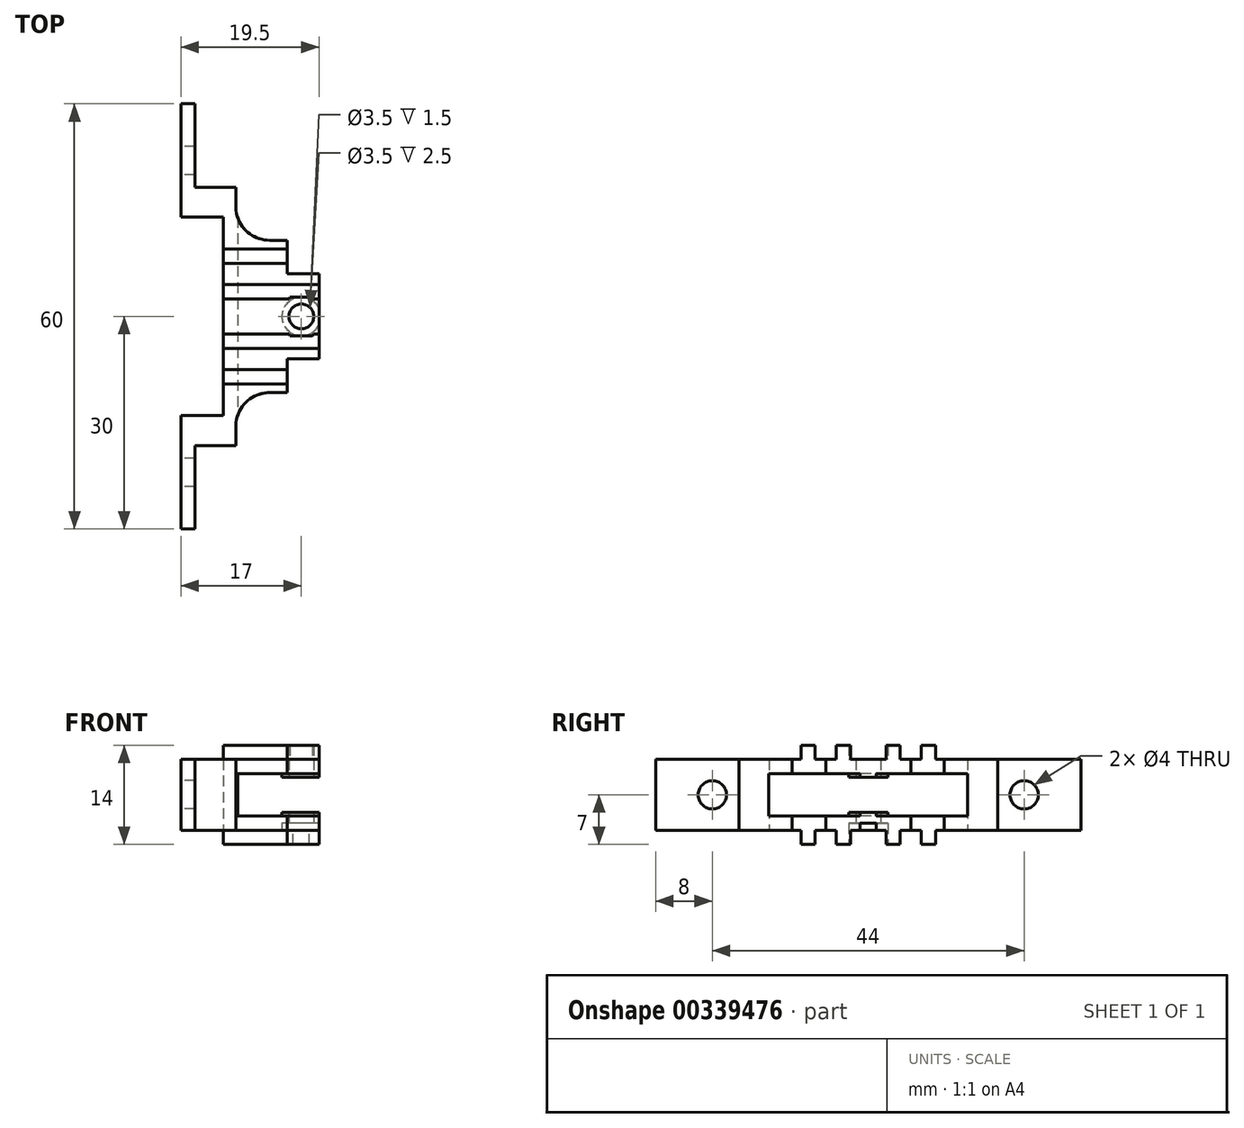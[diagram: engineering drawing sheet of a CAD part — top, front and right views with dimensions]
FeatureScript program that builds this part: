
annotation { "Feature Type Name" : "Feature", "Feature Type Description" : "" }
export const myFeature = defineFeature(function(context is Context, id is Id, definition is map)
    precondition{}
    {
        {
            var Q0;
            Q0=qCreatedBy(makeId("Top.planeOp"),FACE);
            var sketch = newSketch(context, id + "F0", { "sketchPlane" : qUnion([Q0])});
            skLineSegment(sketch, "E0.0", {"start": v(-988.73, -15.3) * mm, "end": v(-988.73, -19.06) * mm});
            skLineSegment(sketch, "E1.MirrorCS", {"start": v(19.5, -4.62) * mm, "end": v(19.5, -6) * mm});
            skLineSegment(sketch, "E2", {"start": v(19.5, -5.89) * mm, "end": v(19.5, 0.89) * mm});
            skLineSegment(sketch, "E3", {"start": v(15, -10.75) * mm, "end": v(15, -7) * mm});
            skLineSegment(sketch, "E4.MirrorCS", {"start": v(2, -30) * mm, "end": v(2, -18.25) * mm});
            skLineSegment(sketch, "E5.0", {"start": v(2, -18.25) * mm, "end": v(7.77, -18.25) * mm});
            skLineSegment(sketch, "E6.0", {"start": v(12.52, -10.75) * mm, "end": v(15, -10.75) * mm});
            skArc(sketch, "E7.0", {"start": v(12.52, -10.75) * mm, "mid": v(9.16, -12.14) * mm, "end": v(7.77, -15.5) * mm});
            skLineSegment(sketch, "E8.0", {"start": v(7.77, -15.5) * mm, "end": v(7.77, -18.25) * mm});
            skLineSegment(sketch, "E9", {"start": v(0, -30) * mm, "end": v(0, 0) * mm});
            skLineSegment(sketch, "E10", {"start": v(2, -30) * mm, "end": v(0, -30) * mm});
            skLineSegment(sketch, "E11.MirrorCS", {"start": v(2, 30) * mm, "end": v(2, 18.25) * mm});
            skLineSegment(sketch, "E12.MirrorCS", {"start": v(0, 30) * mm, "end": v(0, 0) * mm});
            skLineSegment(sketch, "E13.MirrorCS", {"start": v(2, 30) * mm, "end": v(0, 30) * mm});
            skLineSegment(sketch, "E14.MirrorCS", {"start": v(2, 18.25) * mm, "end": v(7.77, 18.25) * mm});
            skLineSegment(sketch, "E15.MirrorCS", {"start": v(7.77, 15.5) * mm, "end": v(7.77, 18.25) * mm});
            skArc(sketch, "E16.MirrorCS", {"start": v(12.52, 10.75) * mm, "mid": v(9.16, 12.14) * mm, "end": v(7.77, 15.5) * mm});
            skLineSegment(sketch, "E17.MirrorCS", {"start": v(12.52, 10.75) * mm, "end": v(15, 10.75) * mm});
            skLineSegment(sketch, "E18.MirrorCS", {"start": v(15, 10.75) * mm, "end": v(15, 7) * mm});
            skLineSegment(sketch, "E19.MirrorCS", {"start": v(19.5, 4.62) * mm, "end": v(19.5, 6) * mm});
            skLineSegment(sketch, "E20.MirrorCS", {"start": v(19.5, 5.89) * mm, "end": v(19.5, 0.89) * mm});
            skLineSegment(sketch, "E21", {"start": v(0, 7.5) * mm, "end": v(15, 7.5) * mm});
            skLineSegment(sketch, "E22", {"start": v(0, 4.5) * mm, "end": v(19.5, 4.5) * mm});
            skLineSegment(sketch, "E23", {"start": v(0, 9.5) * mm, "end": v(15, 9.5) * mm});
            skLineSegment(sketch, "E24", {"start": v(0, 2.5) * mm, "end": v(19.5, 2.5) * mm});
            skLineSegment(sketch, "E25", {"start": v(19.5, 6) * mm, "end": v(15, 6) * mm});
            skLineSegment(sketch, "E26", {"start": v(15, 6) * mm, "end": v(15, 10.75) * mm});
            skLineSegment(sketch, "E27.MirrorCS", {"start": v(0, -2.5) * mm, "end": v(19.5, -2.5) * mm});
            skLineSegment(sketch, "E28.MirrorCS", {"start": v(0, -4.5) * mm, "end": v(19.5, -4.5) * mm});
            skLineSegment(sketch, "E29.MirrorCS", {"start": v(0, -7.5) * mm, "end": v(15, -7.5) * mm});
            skLineSegment(sketch, "E30.MirrorCS", {"start": v(0, -9.5) * mm, "end": v(15, -9.5) * mm});
            skLineSegment(sketch, "E31.MirrorCS", {"start": v(19.5, -6) * mm, "end": v(15, -6) * mm});
            skLineSegment(sketch, "E32.MirrorCS", {"start": v(15, -6) * mm, "end": v(15, -10.75) * mm});
            skPoint(sketch, "E33.orphan", {"position": v(19.5, -0.89) * mm});
            skCircle(sketch, "E34", {"center": v(17, 0) * mm, "radius": 1.75 * mm});
            skCircle(sketch, "E35", {"center": v(17, 0) * mm, "radius": 2.75 * mm});
            skSolve(sketch);
        }
        {
            var Q0;
            Q0=makeQuery(id+"F0.imprint","IMPRINT",FACE,{"disambiguationData":[TD([[makeQuery(id+"F0.imprint","IMPRINT",EDGE,{"derivedFrom":sQuery(id+"F0.wireOp",EDGE,"E4.MirrorCS")}),1.0]])]});
            var Q1;
            Q1=makeQuery(id+"F0.imprint","IMPRINT",FACE,{"disambiguationData":[TD([[makeQuery(id+"F0.imprint","IMPRINT",EDGE,{"derivedFrom":sQuery(id+"F0.wireOp",EDGE,"E11.MirrorCS")}),-1.0]])]});
            var Q2;
            {var subQ4=sQuery(id+"F0.wireOp",EDGE,"E1.MirrorCS");Q2=makeQuery(id+"F0.imprint","IMPRINT",FACE,{"disambiguationData":[TD([[makeQuery(id+"F0.imprint","IMPRINT",EDGE,{"derivedFrom":subQ4}),-1.0]])]});}
            var Q3;
            {var subQ0=sQuery(id+"F0.wireOp",EDGE,"E27.MirrorCS");var subQ1=sQuery(id+"F0.wireOp",EDGE,"E2");var subQ2=makeQuery(id+"F0.imprint","INTERSECT",VERTEX,{"derivedFrom":[subQ1,subQ0]});Q3=makeQuery(id+"F0.imprint","IMPRINT",FACE,{"disambiguationData":[TD([[makeQuery(id+"F0.imprint","IMPRINT",EDGE,{"disambiguationData":[TD([[subQ2,-1.0]])],"derivedFrom":subQ1}),1.0]])]});}
            var Q4;
            {var subQ0=sQuery(id+"F0.wireOp",EDGE,"E29.MirrorCS");Q4=makeQuery(id+"F0.imprint","IMPRINT",FACE,{"disambiguationData":[TD([[makeQuery(id+"F0.imprint","IMPRINT",EDGE,{"derivedFrom":subQ0}),-1.0]])]});}
            var Q5;
            {var subQ0=sQuery(id+"F0.wireOp",EDGE,"E21");Q5=makeQuery(id+"F0.imprint","IMPRINT",FACE,{"disambiguationData":[TD([[makeQuery(id+"F0.imprint","IMPRINT",EDGE,{"derivedFrom":subQ0}),1.0]])]});}
            var Q6;
            {var subQ1=sQuery(id+"F0.wireOp",EDGE,"E19.MirrorCS");Q6=makeQuery(id+"F0.imprint","IMPRINT",FACE,{"disambiguationData":[TD([[makeQuery(id+"F0.imprint","IMPRINT",EDGE,{"derivedFrom":subQ1}),1.0]])]});}
            var Q7;
            {var subQ0=sQuery(id+"F0.wireOp",EDGE,"E24");var subQ1=sQuery(id+"F0.wireOp",EDGE,"E20.MirrorCS");var subQ2=makeQuery(id+"F0.imprint","INTERSECT",VERTEX,{"derivedFrom":[subQ1,subQ0]});Q7=makeQuery(id+"F0.imprint","IMPRINT",FACE,{"disambiguationData":[TD([[makeQuery(id+"F0.imprint","IMPRINT",EDGE,{"disambiguationData":[TD([[subQ2,-1.0]])],"derivedFrom":subQ1}),-1.0]])]});}
            var Q8;
            {var subQ1=sQuery(id+"F0.wireOp",EDGE,"E9");var subQ5=sQuery(id+"F0.wireOp",EDGE,"E12.MirrorCS");var subQ6=makeQuery(id+"F0.imprint","INTERSECT",VERTEX,{"derivedFrom":[subQ1,subQ5]});Q8=makeQuery(id+"F0.imprint","IMPRINT",FACE,{"disambiguationData":[TD([[makeQuery(id+"F0.imprint","IMPRINT",EDGE,{"disambiguationData":[TD([[subQ6,1.0]])],"derivedFrom":subQ1}),-1.0]])]});}
            var Q9;
            {var subQ7=sQuery(id+"F0.wireOp",EDGE,"E28.MirrorCS");Q9=makeQuery(id+"F0.imprint","IMPRINT",FACE,{"disambiguationData":[TD([[makeQuery(id+"F0.imprint","IMPRINT",EDGE,{"derivedFrom":subQ7}),1.0]])]});}
            var Q10;
            {var subQ0=sQuery(id+"F0.wireOp",EDGE,"E22");Q10=makeQuery(id+"F0.imprint","IMPRINT",FACE,{"disambiguationData":[TD([[makeQuery(id+"F0.imprint","IMPRINT",EDGE,{"derivedFrom":subQ0}),-1.0]])]});}
            var Q11;
            Q11=makeQuery(id+"F0.imprint","IMPRINT",FACE,{"disambiguationData":[TD([[makeQuery(id+"F0.imprint","IMPRINT",EDGE,{"derivedFrom":sQuery(id+"F0.wireOp",EDGE,"E34")}),-1.0]])]});
            var Q12;
            Q12=makeQuery(id+"F0.imprint","IMPRINT",FACE,{"disambiguationData":[TD([[makeQuery(id+"F0.imprint","IMPRINT",EDGE,{"derivedFrom":sQuery(id+"F0.wireOp",EDGE,"E34")}),-1.0]])]});
            extrude(context, id + "F1", {"entities" : qUnion([Q0, Q1, Q2, Q3, Q4, Q5, Q6, Q7, Q8, Q9, Q10, Q11, Q12]), "depth" : 2 * mm});
        }
        {
            var Q0;
            {var subQ0=sQuery(id+"F0.wireOp",EDGE,"E29.MirrorCS");Q0=makeQuery(id+"F0.imprint","IMPRINT",FACE,{"disambiguationData":[TD([[makeQuery(id+"F0.imprint","IMPRINT",EDGE,{"derivedFrom":subQ0}),-1.0]])]});}
            var Q1;
            {var subQ5=sQuery(id+"F0.wireOp",EDGE,"E28.MirrorCS");Q1=makeQuery(id+"F0.imprint","IMPRINT",FACE,{"disambiguationData":[TD([[makeQuery(id+"F0.imprint","IMPRINT",EDGE,{"derivedFrom":subQ5}),1.0]])]});}
            var Q2;
            {var subQ0=sQuery(id+"F0.wireOp",EDGE,"E22");Q2=makeQuery(id+"F0.imprint","IMPRINT",FACE,{"disambiguationData":[TD([[makeQuery(id+"F0.imprint","IMPRINT",EDGE,{"derivedFrom":subQ0}),-1.0]])]});}
            var Q3;
            {var subQ0=sQuery(id+"F0.wireOp",EDGE,"E21");Q3=makeQuery(id+"F0.imprint","IMPRINT",FACE,{"disambiguationData":[TD([[makeQuery(id+"F0.imprint","IMPRINT",EDGE,{"derivedFrom":subQ0}),1.0]])]});}
            extrude(context, id + "F2", {"entities" : qUnion([Q0, Q1, Q2, Q3]), "operationType" : NewBodyOperationType.ADD, "oppositeDirection" : true, "depth" : 2 * mm});
        }
        {
            var Q0;
            Q0=makeQuery(id+"F0.imprint","IMPRINT",FACE,{"disambiguationData":[TD([[makeQuery(id+"F0.imprint","IMPRINT",EDGE,{"derivedFrom":sQuery(id+"F0.wireOp",EDGE,"E34")}),-1.0]])]});
            var Q1;
            {var subQ0=sQuery(id+"F0.wireOp",EDGE,"E35");var subQ1=sQuery(id+"F0.wireOp",EDGE,"E27.MirrorCS");var subQ2=makeQuery(id+"F0.imprint","INTERSECT",VERTEX,{"disambiguationData":[OD(0.0)],"derivedFrom":[subQ1,subQ0]});Q1=makeQuery(id+"F0.imprint","IMPRINT",FACE,{"disambiguationData":[TD([[makeQuery(id+"F0.imprint","IMPRINT",EDGE,{"disambiguationData":[TD([[subQ2,-1.0]])],"derivedFrom":subQ1}),-1.0]])]});}
            var Q2;
            {var subQ0=sQuery(id+"F0.wireOp",EDGE,"E35");var subQ1=sQuery(id+"F0.wireOp",EDGE,"E24");var subQ2=makeQuery(id+"F0.imprint","INTERSECT",VERTEX,{"disambiguationData":[OD(0.0)],"derivedFrom":[subQ1,subQ0]});Q2=makeQuery(id+"F0.imprint","IMPRINT",FACE,{"disambiguationData":[TD([[makeQuery(id+"F0.imprint","IMPRINT",EDGE,{"disambiguationData":[TD([[subQ2,-1.0]])],"derivedFrom":subQ1}),1.0]])]});}
            extrude(context, id + "F3", {"entities" : qUnion([Q0, Q1, Q2]), "operationType" : NewBodyOperationType.ADD, "depth" : 2.5 * mm});
        }
        {
            var Q0;
            Q0=makeQuery(id+"F1.opExtrude","CAP_FACE",FACE,{"disambiguationData":[OSD([sQuery(id+"F0.wireOp",EDGE,"E1.MirrorCS"),sQuery(id+"F0.wireOp",EDGE,"E2"),sQuery(id+"F0.wireOp",EDGE,"E4.MirrorCS"),sQuery(id+"F0.wireOp",EDGE,"E5.0"),sQuery(id+"F0.wireOp",EDGE,"E6.0"),sQuery(id+"F0.wireOp",EDGE,"E7.0"),sQuery(id+"F0.wireOp",EDGE,"E8.0"),sQuery(id+"F0.wireOp",EDGE,"E10"),sQuery(id+"F0.wireOp",EDGE,"E9"),sQuery(id+"F0.wireOp",EDGE,"E11.MirrorCS"),sQuery(id+"F0.wireOp",EDGE,"E12.MirrorCS"),sQuery(id+"F0.wireOp",EDGE,"E13.MirrorCS"),sQuery(id+"F0.wireOp",EDGE,"E14.MirrorCS"),sQuery(id+"F0.wireOp",EDGE,"E15.MirrorCS"),sQuery(id+"F0.wireOp",EDGE,"E16.MirrorCS"),sQuery(id+"F0.wireOp",EDGE,"E17.MirrorCS"),sQuery(id+"F0.wireOp",EDGE,"E19.MirrorCS"),sQuery(id+"F0.wireOp",EDGE,"E20.MirrorCS"),sQuery(id+"F0.wireOp",EDGE,"E24"),sQuery(id+"F0.wireOp",EDGE,"E25"),sQuery(id+"F0.wireOp",EDGE,"E26"),sQuery(id+"F0.wireOp",EDGE,"E27.MirrorCS"),sQuery(id+"F0.wireOp",EDGE,"E31.MirrorCS"),sQuery(id+"F0.wireOp",EDGE,"E32.MirrorCS"),sQuery(id+"F0.wireOp",EDGE,"E34"),sQuery(id+"F0.wireOp",EDGE,"E35")])],"isStart":false});
            var sketch = newSketch(context, id + "F4", { "sketchPlane" : qUnion([Q0])});
            skLineSegment(sketch, "E36.MirrorCS", {"start": v(19.5, -4.62) * mm, "end": v(19.5, -6) * mm});
            skLineSegment(sketch, "E37", {"start": v(19.5, -5.89) * mm, "end": v(19.5, 0.89) * mm});
            skLineSegment(sketch, "E38", {"start": v(15, -10.75) * mm, "end": v(15, -7) * mm});
            skLineSegment(sketch, "E39.MirrorCS", {"start": v(2, -30) * mm, "end": v(2, -18.25) * mm});
            skLineSegment(sketch, "E40.0", {"start": v(2, -18.25) * mm, "end": v(7.77, -18.25) * mm});
            skLineSegment(sketch, "E41.0", {"start": v(12.52, -10.75) * mm, "end": v(15, -10.75) * mm});
            skArc(sketch, "E42.0", {"start": v(12.52, -10.75) * mm, "mid": v(9.16, -12.14) * mm, "end": v(7.77, -15.5) * mm});
            skLineSegment(sketch, "E43.0", {"start": v(7.77, -15.5) * mm, "end": v(7.77, -18.25) * mm});
            skLineSegment(sketch, "E44", {"start": v(0, -30) * mm, "end": v(0, -13) * mm});
            skLineSegment(sketch, "E45", {"start": v(2, -30) * mm, "end": v(0, -30) * mm});
            skLineSegment(sketch, "E46.MirrorCS", {"start": v(2, 30) * mm, "end": v(2, 18.25) * mm});
            skLineSegment(sketch, "E47.MirrorCS", {"start": v(0, 30) * mm, "end": v(0, 13) * mm});
            skLineSegment(sketch, "E48.MirrorCS", {"start": v(2, 30) * mm, "end": v(0, 30) * mm});
            skLineSegment(sketch, "E49.MirrorCS", {"start": v(2, 18.25) * mm, "end": v(7.77, 18.25) * mm});
            skLineSegment(sketch, "E50.MirrorCS", {"start": v(7.77, 15.5) * mm, "end": v(7.77, 18.25) * mm});
            skArc(sketch, "E51.MirrorCS", {"start": v(12.52, 10.75) * mm, "mid": v(9.16, 12.14) * mm, "end": v(7.77, 15.5) * mm});
            skLineSegment(sketch, "E52.MirrorCS", {"start": v(12.52, 10.75) * mm, "end": v(15, 10.75) * mm});
            skLineSegment(sketch, "E53.MirrorCS", {"start": v(15, 10.75) * mm, "end": v(15, 7) * mm});
            skLineSegment(sketch, "E54.MirrorCS", {"start": v(19.5, 4.62) * mm, "end": v(19.5, 6) * mm});
            skLineSegment(sketch, "E55.MirrorCS", {"start": v(19.5, 5.89) * mm, "end": v(19.5, 0.89) * mm});
            skLineSegment(sketch, "E56", {"start": v(8, 7.5) * mm, "end": v(15, 7.5) * mm});
            skLineSegment(sketch, "E57", {"start": v(8, 4.5) * mm, "end": v(19.5, 4.5) * mm});
            skLineSegment(sketch, "E58", {"start": v(8, 9.5) * mm, "end": v(15, 9.5) * mm});
            skLineSegment(sketch, "E59", {"start": v(8, 2.5) * mm, "end": v(19.5, 2.5) * mm});
            skLineSegment(sketch, "E60", {"start": v(19.5, 6) * mm, "end": v(15, 6) * mm});
            skLineSegment(sketch, "E61", {"start": v(15, 6) * mm, "end": v(15, 10.75) * mm});
            skLineSegment(sketch, "E62.MirrorCS", {"start": v(8, -2.5) * mm, "end": v(19.5, -2.5) * mm});
            skLineSegment(sketch, "E63.MirrorCS", {"start": v(8, -4.5) * mm, "end": v(19.5, -4.5) * mm});
            skLineSegment(sketch, "E64.MirrorCS", {"start": v(8, -7.5) * mm, "end": v(15, -7.5) * mm});
            skLineSegment(sketch, "E65.MirrorCS", {"start": v(8, -9.5) * mm, "end": v(15, -9.5) * mm});
            skLineSegment(sketch, "E66.MirrorCS", {"start": v(19.5, -6) * mm, "end": v(15, -6) * mm});
            skLineSegment(sketch, "E67.MirrorCS", {"start": v(15, -6) * mm, "end": v(15, -10.75) * mm});
            skPoint(sketch, "E68.orphan", {"position": v(19.5, -0.89) * mm});
            skCircle(sketch, "E69", {"center": v(14.5, 0) * mm, "radius": 1.75 * mm});
            skCircle(sketch, "E70", {"center": v(14.5, 0) * mm, "radius": 2.75 * mm});
            skLineSegment(sketch, "E71", {"start": v(0, -13) * mm, "end": v(6, -13) * mm});
            skLineSegment(sketch, "E72.MirrorCS", {"start": v(0, 13) * mm, "end": v(6, 13) * mm});
            skLineSegment(sketch, "E73", {"start": v(6, 13) * mm, "end": v(6, -13) * mm});
            skLineSegment(sketch, "E74.0", {"start": v(8, 14.03) * mm, "end": v(8, -14.03) * mm});
            skSolve(sketch);
        }
        {
            var Q0;
            {var subQ0=sQuery(id+"F4.wireOp",EDGE,"E71");Q0=makeQuery(id+"F4.imprint","IMPRINT",FACE,{"disambiguationData":[TD([[makeQuery(id+"F4.imprint","IMPRINT",EDGE,{"derivedFrom":subQ0}),1.0]])]});}
            extrude(context, id + "F5", {"entities" : qUnion([Q0]), "operationType" : NewBodyOperationType.REMOVE, "oppositeDirection" : true, "depth" : 7 * mm});
        }
        {
            var Q0;
            Q0=makeQuery(id+"F4.imprint","IMPRINT",FACE,{"disambiguationData":[TD([[makeQuery(id+"F4.imprint","IMPRINT",EDGE,{"derivedFrom":sQuery(id+"F4.wireOp",EDGE,"E39.MirrorCS")}),1.0]])]});
            extrude(context, id + "F6", {"entities" : qUnion([Q0]), "operationType" : NewBodyOperationType.ADD, "depth" : 6 * mm});
        }
        {
            var Q0;
            Q0=makeQuery(id+"F6.opExtrude","CAP_FACE",FACE,{"disambiguationData":[OSD([sQuery(id+"F4.wireOp",EDGE,"E39.MirrorCS"),sQuery(id+"F4.wireOp",EDGE,"E40.0"),sQuery(id+"F4.wireOp",EDGE,"E42.0"),sQuery(id+"F4.wireOp",EDGE,"E43.0"),sQuery(id+"F4.wireOp",EDGE,"E45"),sQuery(id+"F4.wireOp",EDGE,"E44"),sQuery(id+"F4.wireOp",EDGE,"E46.MirrorCS"),sQuery(id+"F4.wireOp",EDGE,"E47.MirrorCS"),sQuery(id+"F4.wireOp",EDGE,"E48.MirrorCS"),sQuery(id+"F4.wireOp",EDGE,"E49.MirrorCS"),sQuery(id+"F4.wireOp",EDGE,"E50.MirrorCS"),sQuery(id+"F4.wireOp",EDGE,"E51.MirrorCS"),sQuery(id+"F4.wireOp",EDGE,"E71"),sQuery(id+"F4.wireOp",EDGE,"E72.MirrorCS"),sQuery(id+"F4.wireOp",EDGE,"E73"),sQuery(id+"F4.wireOp",EDGE,"E74.0")])],"isStart":false});
            var sketch = newSketch(context, id + "F7", { "sketchPlane" : qUnion([Q0])});
            skLineSegment(sketch, "E75.MirrorCS", {"start": v(19.5, -4.62) * mm, "end": v(19.5, -6) * mm});
            skLineSegment(sketch, "E76", {"start": v(19.5, -5.89) * mm, "end": v(19.5, 0.89) * mm});
            skLineSegment(sketch, "E77", {"start": v(15, -10.75) * mm, "end": v(15, -7) * mm});
            skLineSegment(sketch, "E78.MirrorCS", {"start": v(2, -30) * mm, "end": v(2, -18.25) * mm});
            skLineSegment(sketch, "E79.0", {"start": v(2, -18.25) * mm, "end": v(7.77, -18.25) * mm});
            skLineSegment(sketch, "E80.0", {"start": v(12.52, -10.75) * mm, "end": v(15, -10.75) * mm});
            skArc(sketch, "E81.0", {"start": v(12.52, -10.75) * mm, "mid": v(9.16, -12.14) * mm, "end": v(7.77, -15.5) * mm});
            skLineSegment(sketch, "E82.0", {"start": v(7.77, -15.5) * mm, "end": v(7.77, -18.25) * mm});
            skLineSegment(sketch, "E83", {"start": v(0, -30) * mm, "end": v(0, -13) * mm});
            skLineSegment(sketch, "E84", {"start": v(2, -30) * mm, "end": v(0, -30) * mm});
            skLineSegment(sketch, "E85.MirrorCS", {"start": v(2, 30) * mm, "end": v(2, 18.25) * mm});
            skLineSegment(sketch, "E86.MirrorCS", {"start": v(0, 30) * mm, "end": v(0, 13) * mm});
            skLineSegment(sketch, "E87.MirrorCS", {"start": v(2, 30) * mm, "end": v(0, 30) * mm});
            skLineSegment(sketch, "E88.MirrorCS", {"start": v(2, 18.25) * mm, "end": v(7.77, 18.25) * mm});
            skLineSegment(sketch, "E89.MirrorCS", {"start": v(7.77, 15.5) * mm, "end": v(7.77, 18.25) * mm});
            skArc(sketch, "E90.MirrorCS", {"start": v(12.52, 10.75) * mm, "mid": v(9.16, 12.14) * mm, "end": v(7.77, 15.5) * mm});
            skLineSegment(sketch, "E91.MirrorCS", {"start": v(12.52, 10.75) * mm, "end": v(15, 10.75) * mm});
            skLineSegment(sketch, "E92.MirrorCS", {"start": v(15, 10.75) * mm, "end": v(15, 7) * mm});
            skLineSegment(sketch, "E93.MirrorCS", {"start": v(19.5, 4.62) * mm, "end": v(19.5, 6) * mm});
            skLineSegment(sketch, "E94.MirrorCS", {"start": v(19.5, 5.89) * mm, "end": v(19.5, 0.89) * mm});
            skLineSegment(sketch, "E95", {"start": v(19.5, 6) * mm, "end": v(15, 6) * mm});
            skLineSegment(sketch, "E96", {"start": v(15, 6) * mm, "end": v(15, 10.75) * mm});
            skLineSegment(sketch, "E97.MirrorCS", {"start": v(19.5, -6) * mm, "end": v(15, -6) * mm});
            skLineSegment(sketch, "E98.MirrorCS", {"start": v(15, -6) * mm, "end": v(15, -10.75) * mm});
            skPoint(sketch, "E99.orphan", {"position": v(19.5, -0.89) * mm});
            skCircle(sketch, "E100", {"center": v(17, 0) * mm, "radius": 1.75 * mm});
            skCircle(sketch, "E101", {"center": v(17, 0) * mm, "radius": 2.75 * mm});
            skLineSegment(sketch, "E102", {"start": v(0, -13) * mm, "end": v(6, -13) * mm});
            skLineSegment(sketch, "E103.MirrorCS", {"start": v(0, 13) * mm, "end": v(6, 13) * mm});
            skLineSegment(sketch, "E104", {"start": v(6, 13) * mm, "end": v(6, -13) * mm});
            skSolve(sketch);
        }
        {
            var Q0;
            Q0=makeQuery(id+"F7.imprint","IMPRINT",FACE,{"disambiguationData":[TD([[makeQuery(id+"F7.imprint","IMPRINT",EDGE,{"derivedFrom":sQuery(id+"F7.wireOp",EDGE,"E78.MirrorCS")}),1.0]])]});
            var Q1;
            {var subQ6=sQuery(id+"F7.wireOp",EDGE,"E75.MirrorCS");Q1=makeQuery(id+"F7.imprint","IMPRINT",FACE,{"disambiguationData":[TD([[makeQuery(id+"F7.imprint","IMPRINT",EDGE,{"derivedFrom":subQ6}),-1.0]])]});}
            var Q2;
            Q2=makeQuery(id+"F7.imprint","IMPRINT",FACE,{"disambiguationData":[TD([[makeQuery(id+"F7.imprint","IMPRINT",EDGE,{"derivedFrom":sQuery(id+"F7.wireOp",EDGE,"E100")}),-1.0]])]});
            var Q3;
            Q3=makeQuery(id+"F7.imprint","IMPRINT",FACE,{"disambiguationData":[TD([[makeQuery(id+"F7.imprint","IMPRINT",EDGE,{"derivedFrom":sQuery(id+"F7.wireOp",EDGE,"E100")}),-1.0]])]});
            extrude(context, id + "F8", {"entities" : qUnion([Q0, Q1, Q2, Q3]), "operationType" : NewBodyOperationType.ADD, "depth" : 2 * mm});
        }
        {
            var Q0;
            Q0=makeQuery(id+"F7.imprint","IMPRINT",FACE,{"disambiguationData":[TD([[makeQuery(id+"F7.imprint","IMPRINT",EDGE,{"derivedFrom":sQuery(id+"F7.wireOp",EDGE,"E100")}),-1.0]])]});
            extrude(context, id + "F9", {"entities" : qUnion([Q0]), "operationType" : NewBodyOperationType.ADD, "oppositeDirection" : true, "depth" : 0.5 * mm});
        }
        {
            var Q0;
            Q0=makeQuery(id+"F8.opExtrude","CAP_FACE",FACE,{"disambiguationData":[OSD([sQuery(id+"F7.wireOp",EDGE,"E75.MirrorCS"),sQuery(id+"F7.wireOp",EDGE,"E76"),sQuery(id+"F7.wireOp",EDGE,"E78.MirrorCS"),sQuery(id+"F7.wireOp",EDGE,"E79.0"),sQuery(id+"F7.wireOp",EDGE,"E80.0"),sQuery(id+"F7.wireOp",EDGE,"E81.0"),sQuery(id+"F7.wireOp",EDGE,"E82.0"),sQuery(id+"F7.wireOp",EDGE,"E84"),sQuery(id+"F7.wireOp",EDGE,"E83"),sQuery(id+"F7.wireOp",EDGE,"E85.MirrorCS"),sQuery(id+"F7.wireOp",EDGE,"E86.MirrorCS"),sQuery(id+"F7.wireOp",EDGE,"E87.MirrorCS"),sQuery(id+"F7.wireOp",EDGE,"E88.MirrorCS"),sQuery(id+"F7.wireOp",EDGE,"E89.MirrorCS"),sQuery(id+"F7.wireOp",EDGE,"E90.MirrorCS"),sQuery(id+"F7.wireOp",EDGE,"E91.MirrorCS"),sQuery(id+"F7.wireOp",EDGE,"E93.MirrorCS"),sQuery(id+"F7.wireOp",EDGE,"E94.MirrorCS"),sQuery(id+"F7.wireOp",EDGE,"E95"),sQuery(id+"F7.wireOp",EDGE,"E96"),sQuery(id+"F7.wireOp",EDGE,"E97.MirrorCS"),sQuery(id+"F7.wireOp",EDGE,"E98.MirrorCS"),sQuery(id+"F7.wireOp",EDGE,"E100"),sQuery(id+"F7.wireOp",EDGE,"E102"),sQuery(id+"F7.wireOp",EDGE,"E103.MirrorCS"),sQuery(id+"F7.wireOp",EDGE,"E104")])],"isStart":false});
            var sketch = newSketch(context, id + "F10", { "sketchPlane" : qUnion([Q0])});
            skLineSegment(sketch, "E105.MirrorCS", {"start": v(19.5, -4.62) * mm, "end": v(19.5, -6) * mm});
            skLineSegment(sketch, "E106", {"start": v(19.5, -5.89) * mm, "end": v(19.5, 0.89) * mm});
            skLineSegment(sketch, "E107", {"start": v(15, -10.75) * mm, "end": v(15, -7) * mm});
            skLineSegment(sketch, "E108.MirrorCS", {"start": v(2, -30) * mm, "end": v(2, -18.25) * mm});
            skLineSegment(sketch, "E109.0", {"start": v(2, -18.25) * mm, "end": v(7.77, -18.25) * mm});
            skLineSegment(sketch, "E110.0", {"start": v(12.52, -10.75) * mm, "end": v(15, -10.75) * mm});
            skArc(sketch, "E111.0", {"start": v(12.52, -10.75) * mm, "mid": v(9.16, -12.14) * mm, "end": v(7.77, -15.5) * mm});
            skLineSegment(sketch, "E112.0", {"start": v(7.77, -15.5) * mm, "end": v(7.77, -18.25) * mm});
            skLineSegment(sketch, "E113", {"start": v(0, -30) * mm, "end": v(0, -13) * mm});
            skLineSegment(sketch, "E114", {"start": v(2, -30) * mm, "end": v(0, -30) * mm});
            skLineSegment(sketch, "E115.MirrorCS", {"start": v(2, 30) * mm, "end": v(2, 18.25) * mm});
            skLineSegment(sketch, "E116.MirrorCS", {"start": v(0, 30) * mm, "end": v(0, 13) * mm});
            skLineSegment(sketch, "E117.MirrorCS", {"start": v(2, 30) * mm, "end": v(0, 30) * mm});
            skLineSegment(sketch, "E118.MirrorCS", {"start": v(2, 18.25) * mm, "end": v(7.77, 18.25) * mm});
            skLineSegment(sketch, "E119.MirrorCS", {"start": v(7.77, 15.5) * mm, "end": v(7.77, 18.25) * mm});
            skArc(sketch, "E120.MirrorCS", {"start": v(12.52, 10.75) * mm, "mid": v(9.16, 12.14) * mm, "end": v(7.77, 15.5) * mm});
            skLineSegment(sketch, "E121.MirrorCS", {"start": v(12.52, 10.75) * mm, "end": v(15, 10.75) * mm});
            skLineSegment(sketch, "E122.MirrorCS", {"start": v(15, 10.75) * mm, "end": v(15, 7) * mm});
            skLineSegment(sketch, "E123.MirrorCS", {"start": v(19.5, 4.62) * mm, "end": v(19.5, 6) * mm});
            skLineSegment(sketch, "E124.MirrorCS", {"start": v(19.5, 5.89) * mm, "end": v(19.5, 0.89) * mm});
            skLineSegment(sketch, "E125", {"start": v(6, 7.5) * mm, "end": v(15, 7.5) * mm});
            skLineSegment(sketch, "E126", {"start": v(6, 4.5) * mm, "end": v(19.5, 4.5) * mm});
            skLineSegment(sketch, "E127", {"start": v(6, 9.5) * mm, "end": v(15, 9.5) * mm});
            skLineSegment(sketch, "E128", {"start": v(6, 2.5) * mm, "end": v(19.5, 2.5) * mm});
            skLineSegment(sketch, "E129", {"start": v(19.5, 6) * mm, "end": v(15, 6) * mm});
            skLineSegment(sketch, "E130", {"start": v(15, 6) * mm, "end": v(15, 10.75) * mm});
            skLineSegment(sketch, "E131.MirrorCS", {"start": v(6, -2.5) * mm, "end": v(19.5, -2.5) * mm});
            skLineSegment(sketch, "E132.MirrorCS", {"start": v(6, -4.5) * mm, "end": v(19.5, -4.5) * mm});
            skLineSegment(sketch, "E133.MirrorCS", {"start": v(6, -7.5) * mm, "end": v(15, -7.5) * mm});
            skLineSegment(sketch, "E134.MirrorCS", {"start": v(6, -9.5) * mm, "end": v(15, -9.5) * mm});
            skLineSegment(sketch, "E135.MirrorCS", {"start": v(19.5, -6) * mm, "end": v(15, -6) * mm});
            skLineSegment(sketch, "E136.MirrorCS", {"start": v(15, -6) * mm, "end": v(15, -10.75) * mm});
            skPoint(sketch, "E137.orphan", {"position": v(19.5, -0.89) * mm});
            skCircle(sketch, "E138", {"center": v(17, 0) * mm, "radius": 1.75 * mm});
            skLineSegment(sketch, "E139", {"start": v(0, -13) * mm, "end": v(6, -13) * mm});
            skLineSegment(sketch, "E140.MirrorCS", {"start": v(0, 13) * mm, "end": v(6, 13) * mm});
            skLineSegment(sketch, "E141", {"start": v(6, 13) * mm, "end": v(6, -13) * mm});
            skCircle(sketch, "E142.cCircle", {"center": v(17, 0) * mm, "radius": 3.18 * mm, "construction": true});
            skLineSegment(sketch, "E142.0", {"start": v(18.59, -2.75) * mm, "end": v(15.41, -2.75) * mm});
            skLineSegment(sketch, "E142.1", {"start": v(15.41, -2.75) * mm, "end": v(13.82, 0) * mm});
            skLineSegment(sketch, "E142.2", {"start": v(13.82, 0) * mm, "end": v(15.41, 2.75) * mm});
            skLineSegment(sketch, "E142.3", {"start": v(15.41, 2.75) * mm, "end": v(18.59, 2.75) * mm});
            skLineSegment(sketch, "E142.4", {"start": v(18.59, 2.75) * mm, "end": v(20.18, 0) * mm});
            skLineSegment(sketch, "E142.5", {"start": v(20.18, 0) * mm, "end": v(18.59, -2.75) * mm});
            skSolve(sketch);
        }
        {
            var Q0;
            {var subQ0=sQuery(id+"F10.wireOp",EDGE,"E125");Q0=makeQuery(id+"F10.imprint","IMPRINT",FACE,{"disambiguationData":[TD([[makeQuery(id+"F10.imprint","IMPRINT",EDGE,{"derivedFrom":subQ0}),1.0]])]});}
            var Q1;
            {var subQ5=sQuery(id+"F10.wireOp",EDGE,"E126");Q1=makeQuery(id+"F10.imprint","IMPRINT",FACE,{"disambiguationData":[TD([[makeQuery(id+"F10.imprint","IMPRINT",EDGE,{"derivedFrom":subQ5}),-1.0]])]});}
            var Q2;
            {var subQ0=sQuery(id+"F10.wireOp",EDGE,"E132.MirrorCS");Q2=makeQuery(id+"F10.imprint","IMPRINT",FACE,{"disambiguationData":[TD([[makeQuery(id+"F10.imprint","IMPRINT",EDGE,{"derivedFrom":subQ0}),1.0]])]});}
            var Q3;
            {var subQ0=sQuery(id+"F10.wireOp",EDGE,"E133.MirrorCS");Q3=makeQuery(id+"F10.imprint","IMPRINT",FACE,{"disambiguationData":[TD([[makeQuery(id+"F10.imprint","IMPRINT",EDGE,{"derivedFrom":subQ0}),-1.0]])]});}
            extrude(context, id + "F11", {"entities" : qUnion([Q0, Q1, Q2, Q3]), "operationType" : NewBodyOperationType.ADD, "depth" : 2 * mm});
        }
        {
            var Q0;
            {var subQ4=sQuery(id+"F0.wireOp",EDGE,"E27.MirrorCS");var subQ14=sQuery(id+"F0.wireOp",EDGE,"E13.MirrorCS");var subQ15=sQuery(id+"F0.wireOp",EDGE,"E12.MirrorCS");var subQ17=sQuery(id+"F0.wireOp",EDGE,"E9");Q0=makeQuery(id+"F8.boolean.opBoolean","MERGE",FACE,{"derivedFrom":[makeQuery(id+"F6.boolean.opBoolean","MERGE",FACE,{"derivedFrom":[makeQuery(id+"F5.boolean.opBoolean","SPLIT",FACE,{"disambiguationData":[TD([makeQuery(id+"F1.opExtrude","SWEPT_FACE",FACE,{"disambiguationData":[OSD([subQ14])]})])],"derivedFrom":makeQuery(id+"F2.boolean.opBoolean","MERGE",FACE,{"derivedFrom":[makeQuery(id+"F1.opExtrude","SWEPT_FACE",FACE,{"disambiguationData":[OSD([subQ17,subQ15])]}),makeQuery(id+"F2.opExtrude","SWEPT_FACE",FACE,{"disambiguationData":[OSD([subQ17]),TDD([makeQuery(id+"F0.imprint","IMPRINT",EDGE,{"disambiguationData":[TD([[makeQuery(id+"F0.imprint","INTERSECT",VERTEX,{"derivedFrom":[subQ17,sQuery(id+"F0.wireOp",EDGE,"E29.MirrorCS")]}),1.0]])],"derivedFrom":subQ17})])]}),makeQuery(id+"F2.opExtrude","SWEPT_FACE",FACE,{"disambiguationData":[OSD([subQ17]),TDD([makeQuery(id+"F0.imprint","IMPRINT",EDGE,{"disambiguationData":[TD([[makeQuery(id+"F0.imprint","INTERSECT",VERTEX,{"derivedFrom":[subQ17,subQ4]}),1.0]])],"derivedFrom":subQ17})])]}),makeQuery(id+"F2.opExtrude","SWEPT_FACE",FACE,{"disambiguationData":[OSD([subQ15]),TDD([makeQuery(id+"F0.imprint","IMPRINT",EDGE,{"disambiguationData":[TD([[makeQuery(id+"F0.imprint","INTERSECT",VERTEX,{"derivedFrom":[subQ15,sQuery(id+"F0.wireOp",EDGE,"E21")]}),1.0]])],"derivedFrom":subQ15})])]}),makeQuery(id+"F2.opExtrude","SWEPT_FACE",FACE,{"disambiguationData":[OSD([subQ15]),TDD([makeQuery(id+"F0.imprint","IMPRINT",EDGE,{"disambiguationData":[TD([[makeQuery(id+"F0.imprint","INTERSECT",VERTEX,{"derivedFrom":[subQ15,sQuery(id+"F0.wireOp",EDGE,"E22")]}),-1.0]])],"derivedFrom":subQ15})])]})]})}),makeQuery(id+"F6.opExtrude","SWEPT_FACE",FACE,{"disambiguationData":[OSD([sQuery(id+"F4.wireOp",EDGE,"E47.MirrorCS")])]})]}),makeQuery(id+"F8.opExtrude","SWEPT_FACE",FACE,{"disambiguationData":[OSD([sQuery(id+"F7.wireOp",EDGE,"E86.MirrorCS")])]})]});}
            var sketch = newSketch(context, id + "F12", { "sketchPlane" : qUnion([Q0])});
            skCircle(sketch, "E143", {"center": v(-22, 5) * mm, "radius": 2 * mm});
            skCircle(sketch, "E144.MirrorC", {"center": v(22, 5) * mm, "radius": 2 * mm});
            skSolve(sketch);
        }
        {
            var Q0;
            Q0=qSketchRegion(id+"F12",true);
            extrude(context, id + "F13", {"entities" : qUnion([Q0]), "operationType" : NewBodyOperationType.REMOVE, "oppositeDirection" : true, "depth" : 25 * mm});
        }
        {
            var Q0;
            {var subQ0=sQuery(id+"F0.wireOp",EDGE,"E35");var subQ1=sQuery(id+"F0.wireOp",EDGE,"E34");var subQ2=sQuery(id+"F0.wireOp",EDGE,"E27.MirrorCS");var subQ3=sQuery(id+"F0.wireOp",EDGE,"E9");var subQ5=sQuery(id+"F0.wireOp",EDGE,"E24");var subQ9=sQuery(id+"F0.wireOp",EDGE,"E2");var subQ10=sQuery(id+"F0.wireOp",EDGE,"E12.MirrorCS");var subQ11=sQuery(id+"F0.wireOp",EDGE,"E20.MirrorCS");var subQ15=sQuery(id+"F0.wireOp",EDGE,"E19.MirrorCS");var subQ16=sQuery(id+"F0.wireOp",EDGE,"E1.MirrorCS");Q0=makeQuery(id+"F3.boolean.opBoolean","MERGE",FACE,{"derivedFrom":[makeQuery(id+"F2.boolean.opBoolean","SPLIT",FACE,{"disambiguationData":[TD([makeQuery(id+"F1.opExtrude","SWEPT_FACE",FACE,{"disambiguationData":[OSD([subQ5])]})])],"derivedFrom":makeQuery(id+"F1.opExtrude","CAP_FACE",FACE,{"disambiguationData":[OSD([subQ16,subQ9,sQuery(id+"F0.wireOp",EDGE,"E4.MirrorCS"),sQuery(id+"F0.wireOp",EDGE,"E5.0"),sQuery(id+"F0.wireOp",EDGE,"E6.0"),sQuery(id+"F0.wireOp",EDGE,"E7.0"),sQuery(id+"F0.wireOp",EDGE,"E8.0"),sQuery(id+"F0.wireOp",EDGE,"E10"),subQ3,sQuery(id+"F0.wireOp",EDGE,"E11.MirrorCS"),subQ10,sQuery(id+"F0.wireOp",EDGE,"E13.MirrorCS"),sQuery(id+"F0.wireOp",EDGE,"E14.MirrorCS"),sQuery(id+"F0.wireOp",EDGE,"E15.MirrorCS"),sQuery(id+"F0.wireOp",EDGE,"E16.MirrorCS"),sQuery(id+"F0.wireOp",EDGE,"E17.MirrorCS"),subQ15,subQ11,subQ5,sQuery(id+"F0.wireOp",EDGE,"E25"),sQuery(id+"F0.wireOp",EDGE,"E26"),subQ2,sQuery(id+"F0.wireOp",EDGE,"E31.MirrorCS"),sQuery(id+"F0.wireOp",EDGE,"E32.MirrorCS"),subQ1,subQ0])],"isStart":true})}),makeQuery(id+"F3.opExtrude","CAP_FACE",FACE,{"disambiguationData":[OSD([subQ1,subQ0])],"isStart":true})]});}
            var sketch = newSketch(context, id + "F14", { "sketchPlane" : qUnion([Q0])});
            skCircle(sketch, "E145", {"center": v(17, 0) * mm, "radius": 2.75 * mm});
            skSolve(sketch);
        }
        {
            var Q0;
            Q0=makeQuery(id+"F14.imprint","IMPRINT",FACE,{"disambiguationData":[TD([[makeQuery(id+"F14.imprint","IMPRINT",EDGE,{"derivedFrom":makeQuery(id+"F1.opExtrude","CAP_EDGE",EDGE,{"disambiguationData":[OSD([sQuery(id+"F0.wireOp",EDGE,"E34")])],"isStart":true})}),1.0]])]});
            extrude(context, id + "F15", {"entities" : qUnion([Q0]), "operationType" : NewBodyOperationType.REMOVE, "oppositeDirection" : true, "depth" : 1 * mm});
        }
        {
            var Q0;
            Q0=makeQuery(id+"F7.imprint","IMPRINT",FACE,{"disambiguationData":[TD([[makeQuery(id+"F7.imprint","IMPRINT",EDGE,{"derivedFrom":sQuery(id+"F7.wireOp",EDGE,"E78.MirrorCS")}),1.0]])]});
            var sketch = newSketch(context, id + "F16", { "sketchPlane" : qUnion([Q0])});
            skLineSegment(sketch, "E146", {"start": v(0, -14) * mm, "end": v(6, -14) * mm});
            skLineSegment(sketch, "E147", {"start": v(6, 14) * mm, "end": v(0, 14) * mm});
            skLineSegment(sketch, "E148.bottom", {"start": v(6, -14) * mm, "end": v(0, -14) * mm});
            skLineSegment(sketch, "E148.top", {"start": v(6, -13) * mm, "end": v(0, -13) * mm});
            skLineSegment(sketch, "E148.left", {"start": v(6, -14) * mm, "end": v(6, -13) * mm});
            skLineSegment(sketch, "E148.right", {"start": v(0, -14) * mm, "end": v(0, -13) * mm});
            skLineSegment(sketch, "E149.bottom", {"start": v(0, 14) * mm, "end": v(6, 14) * mm});
            skLineSegment(sketch, "E149.top", {"start": v(0, 13) * mm, "end": v(6, 13) * mm});
            skLineSegment(sketch, "E149.left", {"start": v(0, 14) * mm, "end": v(0, 13) * mm});
            skLineSegment(sketch, "E149.right", {"start": v(6, 14) * mm, "end": v(6, 13) * mm});
            skSolve(sketch);
        }
        {
            var Q0;
            Q0 = qSketchRegion(id + "F16", true);
            extrude(context, id + "F17", {"entities" : qUnion([Q0]), "operationType" : NewBodyOperationType.REMOVE, "endBound" : BoundingType.SYMMETRIC, "depth" : 30 * mm});
        }
    });
